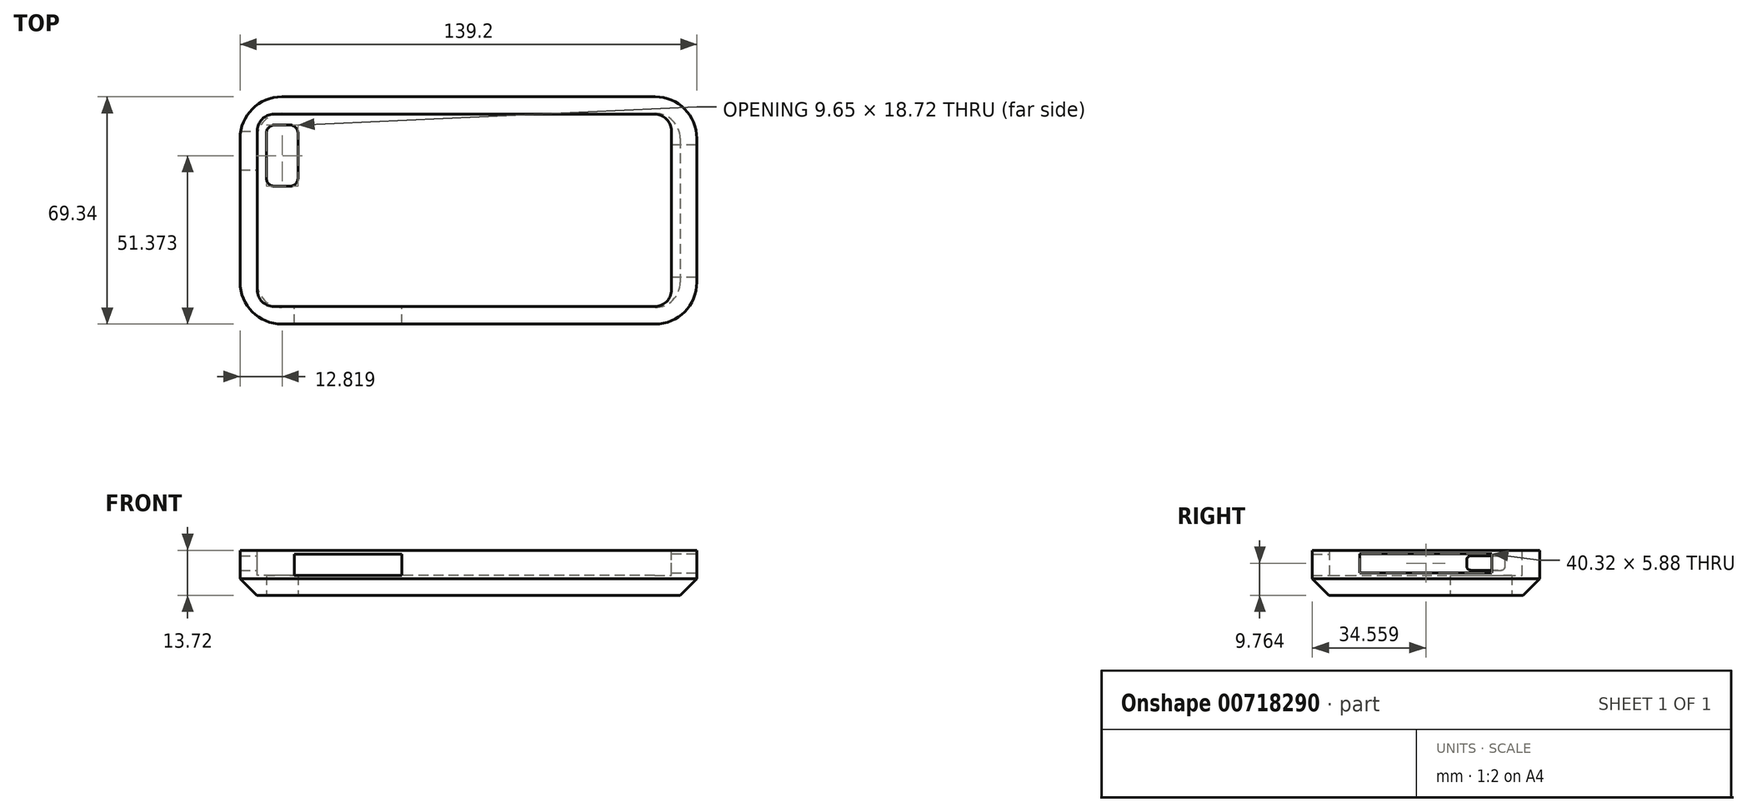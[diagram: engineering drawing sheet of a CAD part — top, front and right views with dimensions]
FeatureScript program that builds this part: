
annotation { "Feature Type Name" : "Feature", "Feature Type Description" : "" }
export const myFeature = defineFeature(function(context is Context, id is Id, definition is map)
    precondition{}
    {
        {
            var Q0;
            Q0=qCreatedBy(makeId("Top.planeOp"),FACE);
            var sketch = newSketch(context, id + "F0", { "sketchPlane" : qUnion([Q0])});
            skLineSegment(sketch, "E0.bottom", {"start": v(69.6, -34.67) * mm, "end": v(-69.6, -34.67) * mm});
            skLineSegment(sketch, "E0.top", {"start": v(69.6, 34.67) * mm, "end": v(-69.6, 34.67) * mm});
            skLineSegment(sketch, "E0.left", {"start": v(69.6, -34.67) * mm, "end": v(69.6, 34.67) * mm});
            skLineSegment(sketch, "E0.right", {"start": v(-69.6, -34.67) * mm, "end": v(-69.6, 34.67) * mm});
            skPoint(sketch, "E0.middle", {"position": v(0, 0) * mm});
            skSolve(sketch);
        }
        {
            var Q0;
            Q0=makeQuery(id+"F0.imprint","IMPRINT",FACE,{"disambiguationData":[TD([[makeQuery(id+"F0.imprint","IMPRINT",EDGE,{"derivedFrom":sQuery(id+"F0.wireOp",EDGE,"E0.bottom")}),-1.0]])]});
            extrude(context, id + "F1", {"entities" : qUnion([Q0]), "depth" : 13.72 * mm, "offsetDistance" : 25.4 * mm});
        }
        {
            var Q0;
            Q0=makeQuery(id+"F1.opExtrude","CAP_FACE",FACE,{"disambiguationData":[OSD([sQuery(id+"F0.wireOp",EDGE,"E0.bottom"),sQuery(id+"F0.wireOp",EDGE,"E0.top"),sQuery(id+"F0.wireOp",EDGE,"E0.left"),sQuery(id+"F0.wireOp",EDGE,"E0.right")])],"isStart":false});
            var sketch = newSketch(context, id + "F2", { "sketchPlane" : qUnion([Q0])});
            skLineSegment(sketch, "E1.bottom", {"start": v(61.85, -29.34) * mm, "end": v(-61.85, -29.34) * mm});
            skLineSegment(sketch, "E1.top", {"start": v(61.85, 29.34) * mm, "end": v(-61.85, 29.34) * mm});
            skLineSegment(sketch, "E1.left", {"start": v(61.85, -29.34) * mm, "end": v(61.85, 29.34) * mm});
            skLineSegment(sketch, "E1.right", {"start": v(-61.85, -29.34) * mm, "end": v(-61.85, 29.34) * mm});
            skPoint(sketch, "E1.middle", {"position": v(0, 0) * mm});
            skSolve(sketch);
        }
        {
            var Q0;
            Q0=makeQuery(id+"F2.imprint","IMPRINT",FACE,{"disambiguationData":[TD([[makeQuery(id+"F2.imprint","IMPRINT",EDGE,{"derivedFrom":sQuery(id+"F2.wireOp",EDGE,"E1.bottom")}),-1.0]])]});
            extrude(context, id + "F3", {"entities" : qUnion([Q0]), "operationType" : NewBodyOperationType.REMOVE, "oppositeDirection" : true, "depth" : 7.62 * mm, "offsetDistance" : 25.4 * mm});
        }
        {
            var Q0;
            Q0=makeQuery(id+"F1.opExtrude","SWEPT_EDGE",EDGE,{"disambiguationData":[OSD([sQuery(id+"F0.wireOp",EDGE,"E0.bottom"),sQuery(id+"F0.wireOp",EDGE,"E0.left")])]});
            fillet(context, id + "F4", {"entities" : qUnion([Q0]), "radius" : 12.7 * mm, "tangentPropagation" : true, "allowEdgeOverflow" : false});
        }
        {
            var Q0;
            Q0=makeQuery(id+"F1.opExtrude","SWEPT_EDGE",EDGE,{"disambiguationData":[OSD([sQuery(id+"F0.wireOp",EDGE,"E0.top"),sQuery(id+"F0.wireOp",EDGE,"E0.left")])]});
            var Q1;
            Q1=makeQuery(id+"F1.opExtrude","SWEPT_EDGE",EDGE,{"disambiguationData":[OSD([sQuery(id+"F0.wireOp",EDGE,"E0.bottom"),sQuery(id+"F0.wireOp",EDGE,"E0.right")])]});
            var Q2;
            Q2=makeQuery(id+"F1.opExtrude","SWEPT_EDGE",EDGE,{"disambiguationData":[OSD([sQuery(id+"F0.wireOp",EDGE,"E0.top"),sQuery(id+"F0.wireOp",EDGE,"E0.right")])]});
            fillet(context, id + "F5", {"entities" : qUnion([Q0, Q1, Q2]), "radius" : 12.7 * mm, "tangentPropagation" : true, "allowEdgeOverflow" : false});
        }
        {
            var Q0;
            Q0=makeQuery(id+"F1.opExtrude","SWEPT_FACE",FACE,{"disambiguationData":[OSD([sQuery(id+"F0.wireOp",EDGE,"E0.left")])]});
            var sketch = newSketch(context, id + "F6", { "sketchPlane" : qUnion([Q0])});
            skLineSegment(sketch, "E2.bottom", {"start": v(-20.27, 6.82) * mm, "end": v(20.05, 6.82) * mm});
            skLineSegment(sketch, "E2.top", {"start": v(-20.27, 12.7) * mm, "end": v(20.05, 12.7) * mm});
            skLineSegment(sketch, "E2.left", {"start": v(-20.27, 6.82) * mm, "end": v(-20.27, 12.7) * mm});
            skLineSegment(sketch, "E2.right", {"start": v(20.05, 6.82) * mm, "end": v(20.05, 12.7) * mm});
            skSolve(sketch);
        }
        {
            var Q0;
            Q0=makeQuery(id+"F6.imprint","IMPRINT",FACE,{"disambiguationData":[TD([[makeQuery(id+"F6.imprint","IMPRINT",EDGE,{"derivedFrom":sQuery(id+"F6.wireOp",EDGE,"E2.bottom")}),1.0]])]});
            extrude(context, id + "F7", {"entities" : qUnion([Q0]), "operationType" : NewBodyOperationType.REMOVE, "oppositeDirection" : true, "depth" : 25.4 * mm, "offsetDistance" : 25.4 * mm});
        }
        {
            var Q0;
            Q0=makeQuery(id+"F3.boolean.opBoolean","COPY",FACE,{"derivedFrom":makeQuery(id+"F3.opExtrude","SWEPT_FACE",FACE,{"disambiguationData":[OSD([sQuery(id+"F2.wireOp",EDGE,"E1.bottom")])]})});
            var sketch = newSketch(context, id + "F8", { "sketchPlane" : qUnion([Q0])});
            skLineSegment(sketch, "E3.bottom", {"start": v(54.92, 6.1) * mm, "end": v(22.1, 6.1) * mm});
            skLineSegment(sketch, "E3.top", {"start": v(54.92, 13.72) * mm, "end": v(22.1, 13.72) * mm});
            skLineSegment(sketch, "E3.left", {"start": v(54.92, 6.1) * mm, "end": v(54.92, 13.72) * mm});
            skLineSegment(sketch, "E3.right", {"start": v(22.1, 6.1) * mm, "end": v(22.1, 13.72) * mm});
            skSolve(sketch);
        }
        {
            var Q0;
            Q0 = qSketchRegion(id + "F8", true);
            extrude(context, id + "F9", {"entities" : qUnion([Q0]), "operationType" : NewBodyOperationType.REMOVE, "oppositeDirection" : true, "depth" : 25.4 * mm, "offsetDistance" : 25.4 * mm});
        }
        {
            var Q0;
            Q0=makeQuery(id+"F9.boolean.opBoolean","COPY",FACE,{"derivedFrom":makeQuery(id+"F9.opExtrude","SWEPT_FACE",FACE,{"disambiguationData":[OSD([sQuery(id+"F8.wireOp",EDGE,"E3.left")])]})});
            var sketch = newSketch(context, id + "F10", { "sketchPlane" : qUnion([Q0])});
            skLineSegment(sketch, "E4.bottom", {"start": v(-34.67, 13.72) * mm, "end": v(-29.34, 13.72) * mm});
            skLineSegment(sketch, "E4.top", {"start": v(-34.67, 12.47) * mm, "end": v(-29.34, 12.47) * mm});
            skLineSegment(sketch, "E4.left", {"start": v(-34.67, 13.72) * mm, "end": v(-34.67, 12.47) * mm});
            skLineSegment(sketch, "E4.right", {"start": v(-29.34, 13.72) * mm, "end": v(-29.34, 12.47) * mm});
            skSolve(sketch);
        }
        {
            var Q0;
            Q0=makeQuery(id+"F10.imprint","IMPRINT",FACE,{"disambiguationData":[TD([[makeQuery(id+"F10.imprint","IMPRINT",EDGE,{"derivedFrom":sQuery(id+"F10.wireOp",EDGE,"E4.bottom")}),-1.0]])]});
            extrude(context, id + "F11", {"entities" : qUnion([Q0]), "operationType" : NewBodyOperationType.ADD, "depth" : 33.02 * mm, "offsetDistance" : 25.4 * mm});
        }
        {
            var Q0;
            Q0=makeQuery(id+"F1.opExtrude","CAP_FACE",FACE,{"disambiguationData":[OSD([sQuery(id+"F0.wireOp",EDGE,"E0.bottom"),sQuery(id+"F0.wireOp",EDGE,"E0.top"),sQuery(id+"F0.wireOp",EDGE,"E0.left"),sQuery(id+"F0.wireOp",EDGE,"E0.right")])],"isStart":true});
            var sketch = newSketch(context, id + "F12", { "sketchPlane" : qUnion([Q0])});
            skLineSegment(sketch, "E5.bottom", {"start": v(-61.6, -26.06) * mm, "end": v(-51.96, -26.06) * mm});
            skLineSegment(sketch, "E5.top", {"start": v(-61.6, -7.34) * mm, "end": v(-51.96, -7.34) * mm});
            skLineSegment(sketch, "E5.left", {"start": v(-61.6, -26.06) * mm, "end": v(-61.6, -7.34) * mm});
            skLineSegment(sketch, "E5.right", {"start": v(-51.96, -26.06) * mm, "end": v(-51.96, -7.34) * mm});
            skSolve(sketch);
        }
        {
            var Q0;
            Q0=makeQuery(id+"F12.imprint","IMPRINT",FACE,{"disambiguationData":[TD([[makeQuery(id+"F12.imprint","IMPRINT",EDGE,{"derivedFrom":sQuery(id+"F12.wireOp",EDGE,"E5.bottom")}),1.0]])]});
            extrude(context, id + "F13", {"entities" : qUnion([Q0]), "operationType" : NewBodyOperationType.REMOVE, "oppositeDirection" : true, "depth" : 25.4 * mm, "offsetDistance" : 25.4 * mm});
        }
        {
            var Q0;
            Q0=makeQuery(id+"F13.boolean.opBoolean","COPY",EDGE,{"derivedFrom":makeQuery(id+"F13.opExtrude","SWEPT_EDGE",EDGE,{"disambiguationData":[OSD([sQuery(id+"F12.wireOp",EDGE,"E5.top"),sQuery(id+"F12.wireOp",EDGE,"E5.right")])]})});
            var Q1;
            Q1=makeQuery(id+"F13.boolean.opBoolean","COPY",EDGE,{"derivedFrom":makeQuery(id+"F13.opExtrude","SWEPT_EDGE",EDGE,{"disambiguationData":[OSD([sQuery(id+"F12.wireOp",EDGE,"E5.bottom"),sQuery(id+"F12.wireOp",EDGE,"E5.left")])]})});
            var Q2;
            Q2=makeQuery(id+"F13.boolean.opBoolean","COPY",EDGE,{"derivedFrom":makeQuery(id+"F13.opExtrude","SWEPT_EDGE",EDGE,{"disambiguationData":[OSD([sQuery(id+"F12.wireOp",EDGE,"E5.top"),sQuery(id+"F12.wireOp",EDGE,"E5.left")])]})});
            var Q3;
            Q3=makeQuery(id+"F13.boolean.opBoolean","COPY",EDGE,{"derivedFrom":makeQuery(id+"F13.opExtrude","SWEPT_EDGE",EDGE,{"disambiguationData":[OSD([sQuery(id+"F12.wireOp",EDGE,"E5.bottom"),sQuery(id+"F12.wireOp",EDGE,"E5.right")])]})});
            fillet(context, id + "F14", {"entities" : qUnion([Q0, Q1, Q2, Q3]), "radius" : 2.54 * mm, "tangentPropagation" : true, "allowEdgeOverflow" : false});
        }
        {
            var Q0;
            Q0=makeQuery(id+"F3.boolean.opBoolean","COPY",FACE,{"derivedFrom":makeQuery(id+"F3.opExtrude","SWEPT_FACE",FACE,{"disambiguationData":[OSD([sQuery(id+"F2.wireOp",EDGE,"E1.right")])]})});
            var sketch = newSketch(context, id + "F15", { "sketchPlane" : qUnion([Q0])});
            skLineSegment(sketch, "E6.bottom", {"start": v(12.35, 7.63) * mm, "end": v(24.1, 7.63) * mm});
            skLineSegment(sketch, "E6.top", {"start": v(12.35, 12.01) * mm, "end": v(24.1, 12.01) * mm});
            skLineSegment(sketch, "E6.left", {"start": v(12.35, 7.63) * mm, "end": v(12.35, 12.01) * mm});
            skLineSegment(sketch, "E6.right", {"start": v(24.1, 7.63) * mm, "end": v(24.1, 12.01) * mm});
            skSolve(sketch);
        }
        {
            var Q0;
            Q0=makeQuery(id+"F15.imprint","IMPRINT",FACE,{"disambiguationData":[TD([[makeQuery(id+"F15.imprint","IMPRINT",EDGE,{"derivedFrom":sQuery(id+"F15.wireOp",EDGE,"E6.bottom")}),1.0]])]});
            extrude(context, id + "F16", {"entities" : qUnion([Q0]), "operationType" : NewBodyOperationType.REMOVE, "oppositeDirection" : true, "depth" : 25.4 * mm, "offsetDistance" : 25.4 * mm});
        }
        {
            var Q0;
            Q0=makeQuery(id+"F16.boolean.opBoolean","COPY",EDGE,{"derivedFrom":makeQuery(id+"F16.opExtrude","SWEPT_EDGE",EDGE,{"disambiguationData":[OSD([sQuery(id+"F15.wireOp",EDGE,"E6.bottom"),sQuery(id+"F15.wireOp",EDGE,"E6.left")])]})});
            var Q1;
            Q1=makeQuery(id+"F16.boolean.opBoolean","COPY",EDGE,{"derivedFrom":makeQuery(id+"F16.opExtrude","SWEPT_EDGE",EDGE,{"disambiguationData":[OSD([sQuery(id+"F15.wireOp",EDGE,"E6.top"),sQuery(id+"F15.wireOp",EDGE,"E6.left")])]})});
            var Q2;
            Q2=makeQuery(id+"F16.boolean.opBoolean","COPY",EDGE,{"derivedFrom":makeQuery(id+"F16.opExtrude","SWEPT_EDGE",EDGE,{"disambiguationData":[OSD([sQuery(id+"F15.wireOp",EDGE,"E6.bottom"),sQuery(id+"F15.wireOp",EDGE,"E6.right")])]})});
            var Q3;
            Q3=makeQuery(id+"F16.boolean.opBoolean","COPY",EDGE,{"derivedFrom":makeQuery(id+"F16.opExtrude","SWEPT_EDGE",EDGE,{"disambiguationData":[OSD([sQuery(id+"F15.wireOp",EDGE,"E6.top"),sQuery(id+"F15.wireOp",EDGE,"E6.right")])]})});
            fillet(context, id + "F17", {"entities" : qUnion([Q0, Q1, Q2, Q3]), "radius" : 1.27 * mm, "tangentPropagation" : true, "allowEdgeOverflow" : false});
        }
        {
            var Q0;
            Q0=makeQuery(id+"F1.opExtrude","CAP_EDGE",EDGE,{"disambiguationData":[OSD([sQuery(id+"F0.wireOp",EDGE,"E0.bottom")])],"isStart":true});
            chamfer(context, id + "F18", {"entities" : qUnion([Q0]), "width" : 5.08 * mm, "tangentPropagation" : true});
        }
        {
            var Q0;
            Q0=makeQuery(id+"F3.boolean.opBoolean","COPY",FACE,{"derivedFrom":makeQuery(id+"F3.opExtrude","SWEPT_FACE",FACE,{"disambiguationData":[OSD([sQuery(id+"F2.wireOp",EDGE,"E1.right")])]})});
            extrude(context, id + "F19", {"entities" : qUnion([Q0]), "operationType" : NewBodyOperationType.REMOVE, "oppositeDirection" : true, "depth" : 2.54 * mm, "offsetDistance" : 25.4 * mm});
        }
        {
            var Q0;
            Q0=makeQuery(id+"F19.boolean.opBoolean","COPY",EDGE,{"derivedFrom":makeQuery(id+"F19.opExtrude","CAP_EDGE",EDGE,{"disambiguationData":[OSD([sQuery(id+"F2.wireOp",EDGE,"E1.bottom"),sQuery(id+"F2.wireOp",EDGE,"E1.right")])],"isStart":false})});
            var Q1;
            Q1=makeQuery(id+"F19.boolean.opBoolean","COPY",EDGE,{"derivedFrom":makeQuery(id+"F19.opExtrude","CAP_EDGE",EDGE,{"disambiguationData":[OSD([sQuery(id+"F2.wireOp",EDGE,"E1.top"),sQuery(id+"F2.wireOp",EDGE,"E1.right")])],"isStart":false})});
            var Q2;
            Q2=makeQuery(id+"F3.boolean.opBoolean","COPY",EDGE,{"derivedFrom":makeQuery(id+"F3.opExtrude","SWEPT_EDGE",EDGE,{"disambiguationData":[OSD([sQuery(id+"F2.wireOp",EDGE,"E1.bottom"),sQuery(id+"F2.wireOp",EDGE,"E1.left")])]})});
            var Q3;
            Q3=makeQuery(id+"F3.boolean.opBoolean","COPY",EDGE,{"derivedFrom":makeQuery(id+"F3.opExtrude","SWEPT_EDGE",EDGE,{"disambiguationData":[OSD([sQuery(id+"F2.wireOp",EDGE,"E1.top"),sQuery(id+"F2.wireOp",EDGE,"E1.left")])]})});
            fillet(context, id + "F20", {"entities" : qUnion([Q0, Q1, Q2, Q3]), "radius" : 5.08 * mm, "tangentPropagation" : true, "allowEdgeOverflow" : false});
        }
        {
            var Q0;
            Q0=makeQuery(id+"F9.boolean.opBoolean","COPY",FACE,{"derivedFrom":makeQuery(id+"F9.opExtrude","SWEPT_FACE",FACE,{"disambiguationData":[OSD([sQuery(id+"F8.wireOp",EDGE,"E3.left")])]})});
            extrude(context, id + "F21", {"entities" : qUnion([Q0]), "operationType" : NewBodyOperationType.ADD, "depth" : 1.78 * mm, "offsetDistance" : 25.4 * mm});
        }
        {
            var Q0;
            Q0=makeQuery(id+"F9.boolean.opBoolean","COPY",FACE,{"derivedFrom":makeQuery(id+"F9.opExtrude","SWEPT_FACE",FACE,{"disambiguationData":[OSD([sQuery(id+"F8.wireOp",EDGE,"E3.right")])]})});
            extrude(context, id + "F22", {"entities" : qUnion([Q0]), "operationType" : NewBodyOperationType.REMOVE, "oppositeDirection" : true, "depth" : 1.78 * mm, "offsetDistance" : 25.4 * mm});
        }
    });
